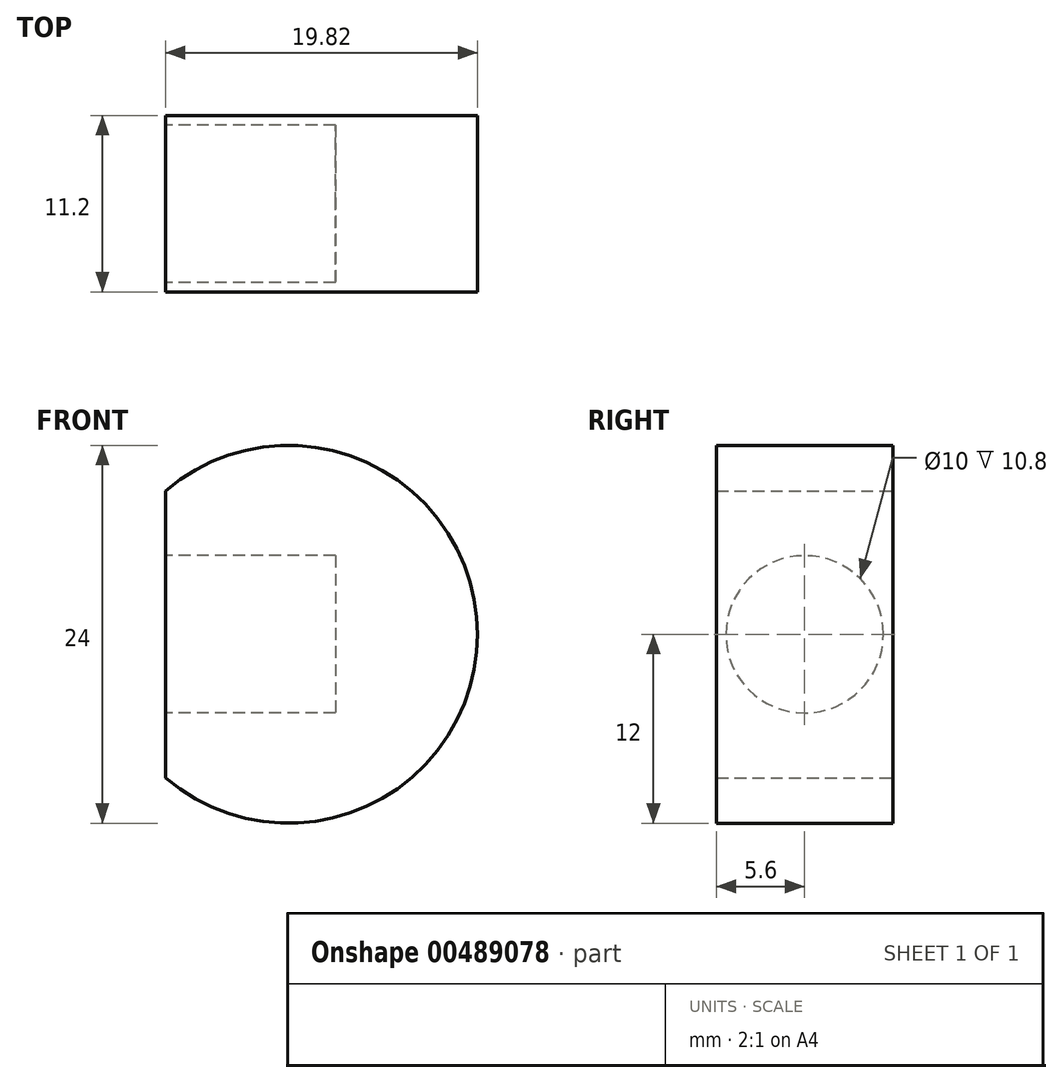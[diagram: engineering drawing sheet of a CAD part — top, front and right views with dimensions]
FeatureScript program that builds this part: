
annotation { "Feature Type Name" : "Feature", "Feature Type Description" : "" }
export const myFeature = defineFeature(function(context is Context, id is Id, definition is map)
    precondition{}
    {
        {
            var Q0;
            Q0=qCreatedBy(makeId("Front.planeOp"),FACE);
            var sketch = newSketch(context, id + "F0", { "sketchPlane" : qUnion([Q0])});
            skLineSegment(sketch, "E0.left", {"start": v(-7.28, -9.1) * mm, "end": v(-7.28, 9.1) * mm});
            skPoint(sketch, "E0.middle", {"position": v(0, 0) * mm});
            skArc(sketch, "E1", {"start": v(-7.28, -9.1) * mm, "mid": v(12.54, 0) * mm, "end": v(-7.28, 9.1) * mm});
            skSolve(sketch);
        }
        {
            var Q0;
            Q0=makeQuery(id+"F0.imprint","IMPRINT",FACE,{"disambiguationData":[TD([[makeQuery(id+"F0.imprint","IMPRINT",EDGE,{"derivedFrom":sQuery(id+"F0.wireOp",EDGE,"E0.left")}),-1.0]])]});
            extrude(context, id + "F1", {"entities" : qUnion([Q0]), "endBound" : BoundingType.SYMMETRIC, "depth" : 11.2 * mm, "offsetDistance" : 25 * mm});
        }
        {
            var Q0;
            Q0=makeQuery(id+"F1.opExtrude","SWEPT_FACE",FACE,{"disambiguationData":[OSD([sQuery(id+"F0.wireOp",EDGE,"E0.left")])]});
            var sketch = newSketch(context, id + "F2", { "sketchPlane" : qUnion([Q0])});
            skCircle(sketch, "E2", {"center": v(0, 0) * mm, "radius": 5 * mm});
            skSolve(sketch);
        }
        {
            var Q0;
            Q0=makeQuery(id+"F2.imprint","IMPRINT",FACE,{"disambiguationData":[TD([[makeQuery(id+"F2.imprint","IMPRINT",EDGE,{"derivedFrom":sQuery(id+"F2.wireOp",EDGE,"E2")}),1.0]])]});
            extrude(context, id + "F3", {"entities" : qUnion([Q0]), "operationType" : NewBodyOperationType.REMOVE, "oppositeDirection" : true, "depth" : 10.8 * mm, "offsetDistance" : 25 * mm});
        }
    });
